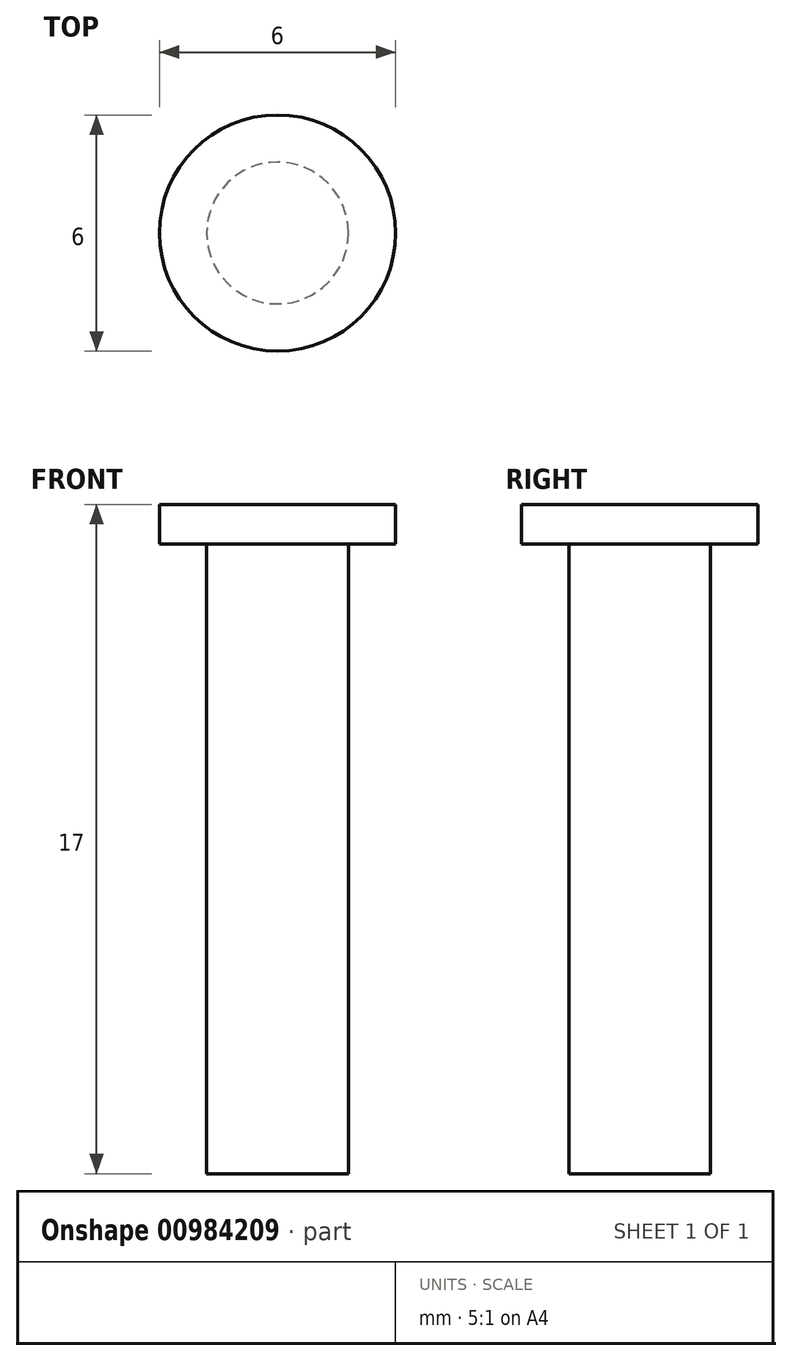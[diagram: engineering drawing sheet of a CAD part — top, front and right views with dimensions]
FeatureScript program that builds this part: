
annotation { "Feature Type Name" : "Feature", "Feature Type Description" : "" }
export const myFeature = defineFeature(function(context is Context, id is Id, definition is map)
    precondition{}
    {
        {
            var Q0;
            Q0=qCreatedBy(makeId("Top.planeOp"),FACE);
            var sketch = newSketch(context, id + "F0", { "sketchPlane" : qUnion([Q0])});
            skCircle(sketch, "E0", {"center": v(0, 0) * mm, "radius": 1.8 * mm});
            skCircle(sketch, "E1.0", {"center": v(0, 0) * mm, "radius": 9.5 * mm});
            skCircle(sketch, "E2.0", {"center": v(0, 0) * mm, "radius": 9.1 * mm});
            skCircle(sketch, "E3", {"center": v(0, 0) * mm, "radius": 3 * mm});
            skSolve(sketch);
        }
        {
            var Q0;
            Q0=makeQuery(id+"F0.imprint","IMPRINT",FACE,{"disambiguationData":[TD([[makeQuery(id+"F0.imprint","IMPRINT",EDGE,{"derivedFrom":sQuery(id+"F0.wireOp",EDGE,"E0")}),1.0]])]});
            extrude(context, id + "F1", {"entities" : qUnion([Q0]), "depth" : 23 * mm, "offsetDistance" : 25 * mm, "hasSecondDirection" : true, "secondDirectionOppositeDirection" : false, "secondDirectionDepth" : 6 * mm});
        }
        {
            var Q0;
            Q0=makeQuery(id+"F0.imprint","IMPRINT",FACE,{"disambiguationData":[TD([[makeQuery(id+"F0.imprint","IMPRINT",EDGE,{"derivedFrom":sQuery(id+"F0.wireOp",EDGE,"E0")}),-1.0]])]});
            extrude(context, id + "F2", {"entities" : qUnion([Q0]), "operationType" : NewBodyOperationType.ADD, "depth" : 23 * mm, "offsetDistance" : 25 * mm, "hasSecondDirection" : true, "secondDirectionOppositeDirection" : false, "secondDirectionDepth" : 22 * mm});
        }
    });
